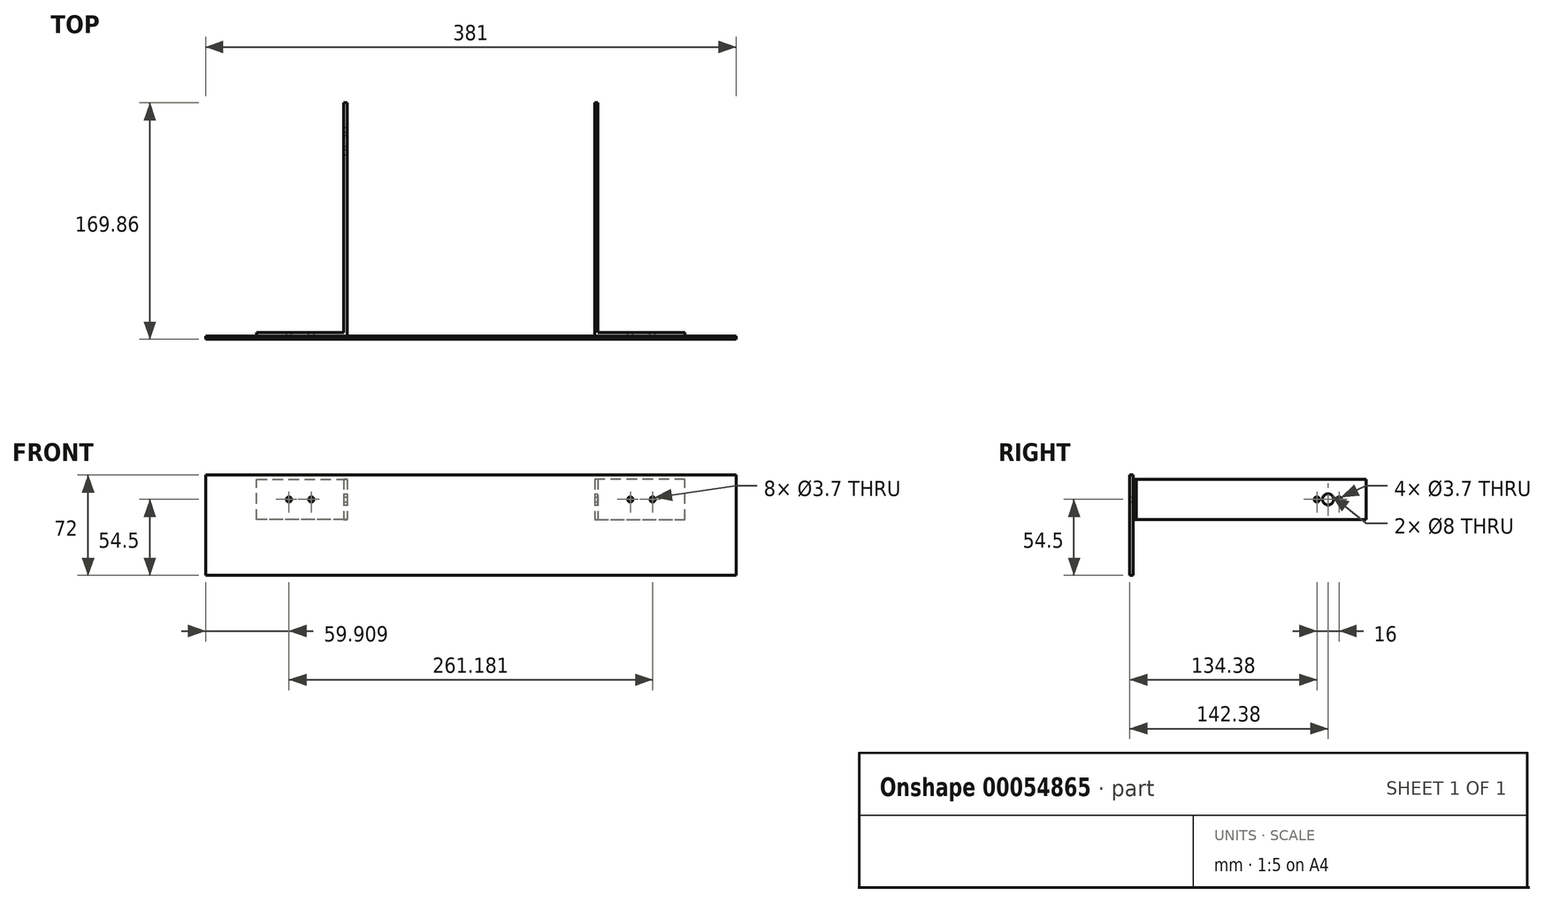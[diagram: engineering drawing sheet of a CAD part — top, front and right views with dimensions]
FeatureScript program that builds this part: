
annotation { "Feature Type Name" : "Feature", "Feature Type Description" : "" }
export const myFeature = defineFeature(function(context is Context, id is Id, definition is map)
    precondition{}
    {
        {
            var Q0;
            Q0=qCreatedBy(makeId("Front.planeOp"),FACE);
            var sketch = newSketch(context, id + "F0", { "sketchPlane" : qUnion([Q0])});
            skLineSegment(sketch, "E0.rect.bottom", {"start": v(190.5, 36) * mm, "end": v(-190.5, 36) * mm});
            skLineSegment(sketch, "E0.rect.top", {"start": v(190.5, -36) * mm, "end": v(-190.5, -36) * mm});
            skLineSegment(sketch, "E0.rect.left", {"start": v(190.5, 36) * mm, "end": v(190.5, -36) * mm});
            skLineSegment(sketch, "E0.rect.right", {"start": v(-190.5, 36) * mm, "end": v(-190.5, -36) * mm});
            skPoint(sketch, "E0.rect.middle", {"position": v(0, 0) * mm});
            skSolve(sketch);
        }
        {
            var Q0;
            Q0=makeQuery(id+"F0.imprint","IMPRINT",FACE,{"disambiguationData":[TD([[makeQuery(id+"F0.imprint","IMPRINT",EDGE,{"derivedFrom":sQuery(id+"F0.wireOp",EDGE,"E0.rect.bottom")}),1.0]])]});
            extrude(context, id + "F1", {"entities" : qUnion([Q0]), "depth" : 2.38 * mm});
        }
        {
            var Q0;
            Q0=makeQuery(id+"F1.opExtrude","CAP_FACE",FACE,{"disambiguationData":[OSD([sQuery(id+"F0.wireOp",EDGE,"E0.rect.bottom"),sQuery(id+"F0.wireOp",EDGE,"E0.rect.top"),sQuery(id+"F0.wireOp",EDGE,"E0.rect.left"),sQuery(id+"F0.wireOp",EDGE,"E0.rect.right")])],"isStart":true});
            var sketch = newSketch(context, id + "F2", { "sketchPlane" : qUnion([Q0])});
            skPoint(sketch, "E1", {"position": v(-88.9, 4) * mm});
            skLineSegment(sketch, "E2.bottom", {"start": v(-88.9, 4) * mm, "end": v(-153.9, 4) * mm});
            skLineSegment(sketch, "E3", {"start": v(-153.9, 4) * mm, "end": v(-153.9, 33) * mm});
            skLineSegment(sketch, "E4", {"start": v(-153.9, 33) * mm, "end": v(-88.9, 33) * mm});
            skLineSegment(sketch, "E5", {"start": v(-88.9, 33) * mm, "end": v(-88.9, 4) * mm});
            skLineSegment(sketch, "E6.MirrorCS", {"start": v(153.9, 33) * mm, "end": v(88.9, 33) * mm});
            skLineSegment(sketch, "E7.MirrorCS", {"start": v(88.9, 33) * mm, "end": v(88.9, 4) * mm});
            skLineSegment(sketch, "E8.MirrorCS", {"start": v(88.9, 4) * mm, "end": v(153.9, 4) * mm});
            skLineSegment(sketch, "E9.MirrorCS", {"start": v(153.9, 4) * mm, "end": v(153.9, 33) * mm});
            skPoint(sketch, "E10.MirrorP", {"position": v(88.9, 4) * mm});
            skSolve(sketch);
        }
        {
            var Q0;
            Q0 = qSketchRegion(id + "F2", true);
            extrude(context, id + "F3", {"entities" : qUnion([Q0]), "depth" : 2.38 * mm});
        }
        {
            var Q0;
            Q0=makeQuery(id+"F3.opExtrude","CAP_FACE",FACE,{"disambiguationData":[OSD([sQuery(id+"F2.wireOp",EDGE,"E2.bottom"),sQuery(id+"F2.wireOp",EDGE,"E3"),sQuery(id+"F2.wireOp",EDGE,"E4"),sQuery(id+"F2.wireOp",EDGE,"E5")])],"isStart":false});
            var sketch = newSketch(context, id + "F4", { "sketchPlane" : qUnion([Q0])});
            skLineSegment(sketch, "E11", {"start": v(-91.28, 33) * mm, "end": v(-91.28, 4) * mm});
            skLineSegment(sketch, "E12", {"start": v(-91.28, 4) * mm, "end": v(-88.9, 4) * mm});
            skLineSegment(sketch, "E13", {"start": v(-88.9, 4) * mm, "end": v(-88.9, 33) * mm});
            skLineSegment(sketch, "E14", {"start": v(-88.9, 33) * mm, "end": v(-91.28, 33) * mm});
            skLineSegment(sketch, "E15.MirrorCS", {"start": v(91.28, 4) * mm, "end": v(88.9, 4) * mm});
            skLineSegment(sketch, "E16.MirrorCS", {"start": v(88.9, 33) * mm, "end": v(91.28, 33) * mm});
            skLineSegment(sketch, "E17.MirrorCS", {"start": v(91.28, 33) * mm, "end": v(91.28, 4) * mm});
            skLineSegment(sketch, "E18.MirrorCS", {"start": v(88.9, 4) * mm, "end": v(88.9, 33) * mm});
            skSolve(sketch);
        }
        {
            var Q0;
            Q0 = qSketchRegion(id + "F4", true);
            extrude(context, id + "F5", {"entities" : qUnion([Q0]), "operationType" : NewBodyOperationType.ADD, "depth" : 165.1 * mm});
        }
        {
            var Q0;
            Q0=makeQuery(id+"F3.opExtrude","CAP_FACE",FACE,{"disambiguationData":[OSD([sQuery(id+"F2.wireOp",EDGE,"E2.bottom"),sQuery(id+"F2.wireOp",EDGE,"E3"),sQuery(id+"F2.wireOp",EDGE,"E4"),sQuery(id+"F2.wireOp",EDGE,"E5")])],"isStart":false});
            var sketch = newSketch(context, id + "F6", { "sketchPlane" : qUnion([Q0])});
            skPoint(sketch, "E19", {"position": v(-122.6, 18.5) * mm});
            skPoint(sketch, "E20.orphan", {"position": v(-91.28, 33) * mm});
            skPoint(sketch, "E21.end.orphan", {"position": v(-153.9, 4) * mm});
            skCircle(sketch, "E22", {"center": v(-130.6, 18.5) * mm, "radius": 1.85 * mm});
            skCircle(sketch, "E23", {"center": v(-114.6, 18.5) * mm, "radius": 1.85 * mm});
            skCircle(sketch, "E24.MirrorC", {"center": v(130.6, 18.5) * mm, "radius": 1.85 * mm});
            skCircle(sketch, "E25.MirrorC", {"center": v(114.6, 18.5) * mm, "radius": 1.85 * mm});
            skPoint(sketch, "E26.MirrorP", {"position": v(153.9, 4) * mm});
            skPoint(sketch, "E27.MirrorP", {"position": v(91.28, 33) * mm});
            skPoint(sketch, "E28.MirrorP", {"position": v(122.6, 18.5) * mm});
            skSolve(sketch);
        }
        {
            var Q0;
            Q0 = qSketchRegion(id + "F6", true);
            extrude(context, id + "F7", {"entities" : qUnion([Q0]), "operationType" : NewBodyOperationType.REMOVE, "oppositeDirection" : true, "depth" : 25 * mm});
        }
        {
            var Q0;
            Q0=makeQuery(id+"F5.opExtrude","SWEPT_FACE",FACE,{"disambiguationData":[OSD([sQuery(id+"F4.wireOp",EDGE,"E11")])]});
            var sketch = newSketch(context, id + "F8", { "sketchPlane" : qUnion([Q0])});
            skPoint(sketch, "E29", {"position": v(140, 18.5) * mm});
            skPoint(sketch, "E29.positionSnap0", {"position": v(2.38, 18.5) * mm});
            skCircle(sketch, "E30", {"center": v(148, 18.5) * mm, "radius": 1.85 * mm});
            skCircle(sketch, "E31", {"center": v(132, 18.5) * mm, "radius": 1.85 * mm});
            skCircle(sketch, "E32", {"center": v(140, 18.5) * mm, "radius": 4 * mm});
            skSolve(sketch);
        }
        {
            var Q0;
            Q0 = qSketchRegion(id + "F8", true);
            extrude(context, id + "F9", {"entities" : qUnion([Q0]), "operationType" : NewBodyOperationType.REMOVE, "oppositeDirection" : true, "depth" : 293.97 * mm});
        }
    });
